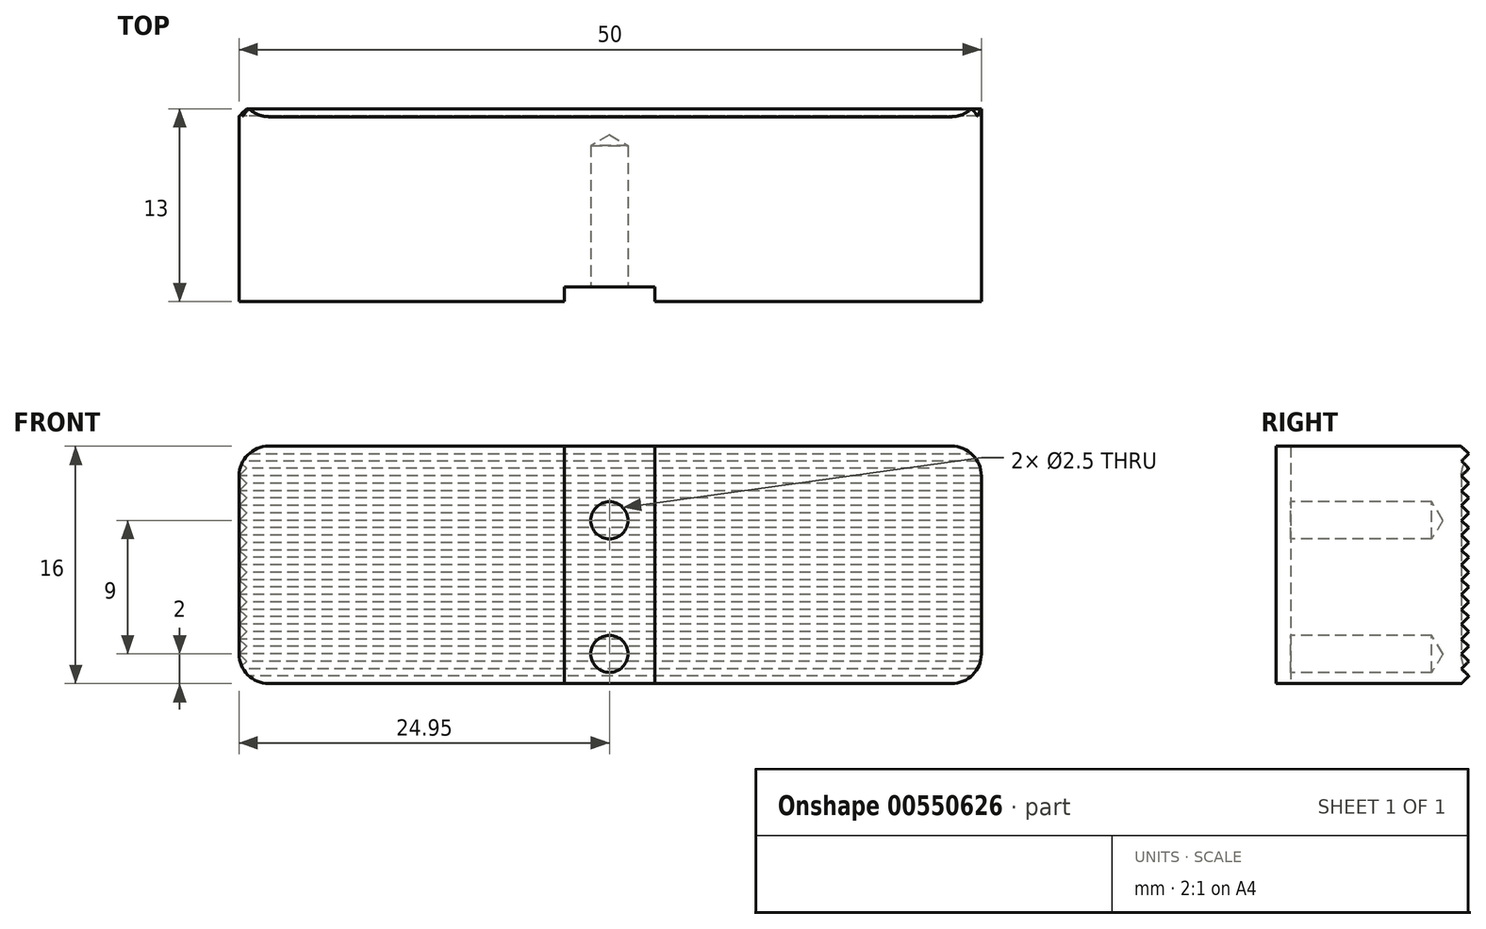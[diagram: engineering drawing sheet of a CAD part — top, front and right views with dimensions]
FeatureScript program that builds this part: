
annotation { "Feature Type Name" : "Feature", "Feature Type Description" : "" }
export const myFeature = defineFeature(function(context is Context, id is Id, definition is map)
    precondition{}
    {
        {
            var Q0;
            Q0=qCreatedBy(makeId("Front.planeOp"),FACE);
            var sketch = newSketch(context, id + "F0", { "sketchPlane" : qUnion([Q0])});
            skLineSegment(sketch, "E0.bottom", {"start": v(0, 0) * mm, "end": v(50, 0) * mm});
            skLineSegment(sketch, "E0.top", {"start": v(0, 16) * mm, "end": v(50, 16) * mm});
            skLineSegment(sketch, "E0.left", {"start": v(0, 0) * mm, "end": v(0, 16) * mm});
            skLineSegment(sketch, "E0.right", {"start": v(50, 0) * mm, "end": v(50, 16) * mm});
            skSolve(sketch);
        }
        {
            var Q0;
            Q0=makeQuery(id+"F0.imprint","IMPRINT",FACE,{"disambiguationData":[TD([[makeQuery(id+"F0.imprint","IMPRINT",EDGE,{"derivedFrom":sQuery(id+"F0.wireOp",EDGE,"E0.bottom")}),1.0]])]});
            extrude(context, id + "F1", {"entities" : qUnion([Q0]), "depth" : 13 * mm, "offsetDistance" : 25 * mm});
        }
        {
            var Q0;
            Q0=makeQuery(id+"F1.opExtrude","CAP_FACE",FACE,{"disambiguationData":[OSD([sQuery(id+"F0.wireOp",EDGE,"E0.bottom"),sQuery(id+"F0.wireOp",EDGE,"E0.top"),sQuery(id+"F0.wireOp",EDGE,"E0.left"),sQuery(id+"F0.wireOp",EDGE,"E0.right")])],"isStart":false});
            var sketch = newSketch(context, id + "F2", { "sketchPlane" : qUnion([Q0])});
            skLineSegment(sketch, "E1.bottom", {"start": v(21.9, 16) * mm, "end": v(28, 16) * mm});
            skLineSegment(sketch, "E1.top", {"start": v(21.9, -2) * mm, "end": v(28, -2) * mm});
            skLineSegment(sketch, "E1.left", {"start": v(21.9, 16) * mm, "end": v(21.9, -2) * mm});
            skLineSegment(sketch, "E1.right", {"start": v(28, 16) * mm, "end": v(28, -2) * mm});
            skSolve(sketch);
        }
        {
            var Q0;
            {var subQ0=sQuery(id+"F2.wireOp",EDGE,"E1.top");Q0=makeQuery(id+"F2.imprint","IMPRINT",FACE,{"disambiguationData":[TD([[makeQuery(id+"F2.imprint","IMPRINT",EDGE,{"derivedFrom":subQ0}),1.0]])]});}
            var Q1;
            {var subQ0=sQuery(id+"F2.wireOp",EDGE,"E1.bottom");Q1=makeQuery(id+"F2.imprint","IMPRINT",FACE,{"disambiguationData":[TD([[makeQuery(id+"F2.imprint","IMPRINT",EDGE,{"derivedFrom":subQ0}),-1.0]])]});}
            extrude(context, id + "F3", {"entities" : qUnion([Q0, Q1]), "operationType" : NewBodyOperationType.REMOVE, "oppositeDirection" : true, "depth" : 1 * mm, "offsetDistance" : 25 * mm});
        }
        {
            var Q0;
            Q0=makeQuery(id+"F3.boolean.opBoolean","COPY",FACE,{"derivedFrom":makeQuery(id+"F3.opExtrude","CAP_FACE",FACE,{"disambiguationData":[OSD([sQuery(id+"F2.wireOp",EDGE,"E1.bottom"),sQuery(id+"F2.wireOp",EDGE,"E1.top"),sQuery(id+"F2.wireOp",EDGE,"E1.left"),sQuery(id+"F2.wireOp",EDGE,"E1.right")])],"isStart":false})});
            var sketch = newSketch(context, id + "F4", { "sketchPlane" : qUnion([Q0])});
            skPoint(sketch, "E2", {"position": v(24.95, 11) * mm});
            skPoint(sketch, "E2.positionSnap0", {"position": v(24.95, 16) * mm});
            skPoint(sketch, "E3", {"position": v(24.95, 2) * mm});
            skSolve(sketch);
        }
        {
            var Q0;
            Q0=sQuery(id+"F4.wireOp",VERTEX,"E2");
            var Q1;
            Q1=sQuery(id+"F4.wireOp",VERTEX,"E3");
            var Q2;
            Q2=makeQuery(id+"F1.opExtrude","SWEPT_BODY",BODY,{"disambiguationData":[OSD([sQuery(id+"F0.wireOp",EDGE,"E0.bottom"),sQuery(id+"F0.wireOp",EDGE,"E0.top"),sQuery(id+"F0.wireOp",EDGE,"E0.left"),sQuery(id+"F0.wireOp",EDGE,"E0.right")])]});
            hole(context, id + "F5", {"style" : HoleStyle.SIMPLE, "endStyle" : HoleEndStyle.BLIND, "standardTappedOrClearance" : lookupTablePath({ "standard" : "ISO", "engagement" : "75%", "pitch" : "0.5 mm", "size" : "M3", "type" : "Tapped" }), "standardBlindInLast" : lookupTablePath({ "standard" : "ISO", "engagement" : "75%", "pitch" : "0.5 mm", "size" : "M3", "type" : "Tapped" }), "holeDiameter" : 2.5 * mm, "showTappedDepth" : true, "holeDepth" : 9.5 * mm, "isTappedThrough" : true, "tappedDepth" : 8 * mm, "tapClearance" : 3, "startFromSketch" : true, "locations" : qUnion([Q0, Q1]), "scope" : qUnion([Q2]), "majorDiameter" : 3 * mm});
        }
        {
            var Q0;
            Q0=makeQuery(id+"F1.opExtrude","CAP_EDGE",EDGE,{"disambiguationData":[OSD([sQuery(id+"F0.wireOp",EDGE,"E0.left")])],"isStart":true});
            var Q1;
            Q1=makeQuery(id+"F1.opExtrude","CAP_EDGE",EDGE,{"disambiguationData":[OSD([sQuery(id+"F0.wireOp",EDGE,"E0.top")])],"isStart":true});
            var Q2;
            Q2=makeQuery(id+"F1.opExtrude","CAP_EDGE",EDGE,{"disambiguationData":[OSD([sQuery(id+"F0.wireOp",EDGE,"E0.bottom")])],"isStart":true});
            chamfer(context, id + "F6", {"entities" : qUnion([Q0, Q1, Q2]), "width" : .5 * mm, "tangentPropagation" : true});
        }
        {
            var Q0;
            Q0=makeQuery(id+"F1.opExtrude","SWEPT_FACE",FACE,{"disambiguationData":[OSD([sQuery(id+"F0.wireOp",EDGE,"E0.left")])]});
            var sketch = newSketch(context, id + "F7", { "sketchPlane" : qUnion([Q0])});
            skPoint(sketch, "E4", {"position": v(0, 0.5) * mm});
            skPoint(sketch, "E5", {"position": v(0.5, 1) * mm});
            skPoint(sketch, "E6", {"position": v(0, 1.5) * mm});
            skPoint(sketch, "E7", {"position": v(0, 2.5) * mm});
            skPoint(sketch, "E8", {"position": v(0, 3.5) * mm});
            skPoint(sketch, "E9", {"position": v(0, 4.5) * mm});
            skPoint(sketch, "E10", {"position": v(0, 5.5) * mm});
            skPoint(sketch, "E11", {"position": v(0, 6.5) * mm});
            skPoint(sketch, "E12", {"position": v(0, 7.5) * mm});
            skPoint(sketch, "E13", {"position": v(0, 9.5) * mm});
            skPoint(sketch, "E14", {"position": v(0, 8.5) * mm});
            skPoint(sketch, "E15", {"position": v(0, 10.5) * mm});
            skPoint(sketch, "E16", {"position": v(0, 11.5) * mm});
            skPoint(sketch, "E17", {"position": v(0, 12.5) * mm});
            skPoint(sketch, "E18", {"position": v(0, 13.5) * mm});
            skPoint(sketch, "E19", {"position": v(0, 14.5) * mm});
            skPoint(sketch, "E20", {"position": v(0, 15.5) * mm});
            skPoint(sketch, "E21", {"position": v(0.5, 2) * mm});
            skPoint(sketch, "E22", {"position": v(0.5, 3) * mm});
            skPoint(sketch, "E23", {"position": v(0.5, 4) * mm});
            skPoint(sketch, "E24", {"position": v(0.5, 5) * mm});
            skPoint(sketch, "E25", {"position": v(0.5, 6) * mm});
            skPoint(sketch, "E26", {"position": v(0.5, 7) * mm});
            skPoint(sketch, "E27", {"position": v(0.5, 8) * mm});
            skPoint(sketch, "E28", {"position": v(0.5, 9) * mm});
            skPoint(sketch, "E29", {"position": v(0.5, 10) * mm});
            skPoint(sketch, "E30", {"position": v(0.5, 11) * mm});
            skPoint(sketch, "E31", {"position": v(0.5, 12) * mm});
            skPoint(sketch, "E32", {"position": v(0.5, 13) * mm});
            skPoint(sketch, "E33", {"position": v(0.5, 14) * mm});
            skPoint(sketch, "E34", {"position": v(0.5, 15) * mm});
            skPoint(sketch, "E35", {"position": v(0.53, 16) * mm});
            skPoint(sketch, "E36", {"position": v(0, 16.5) * mm});
            skLineSegment(sketch, "E37", {"start": v(0, 0.5) * mm, "end": v(0, 16.5) * mm});
            skLineSegment(sketch, "E38", {"start": v(0, 0.5) * mm, "end": v(0.5, 1) * mm});
            skLineSegment(sketch, "E39", {"start": v(0, 1.5) * mm, "end": v(0.5, 2) * mm});
            skLineSegment(sketch, "E40", {"start": v(0.5, 1) * mm, "end": v(0, 1.5) * mm});
            skLineSegment(sketch, "E41", {"start": v(0, 2.5) * mm, "end": v(0.5, 3) * mm});
            skLineSegment(sketch, "E42", {"start": v(0.5, 2) * mm, "end": v(0, 2.5) * mm});
            skLineSegment(sketch, "E43", {"start": v(0.5, 3) * mm, "end": v(0, 3.5) * mm});
            skLineSegment(sketch, "E44", {"start": v(0.5, 4) * mm, "end": v(0, 4.5) * mm});
            skLineSegment(sketch, "E45", {"start": v(0, 3.5) * mm, "end": v(0.5, 4) * mm});
            skLineSegment(sketch, "E46", {"start": v(0, 4.5) * mm, "end": v(0.5, 5) * mm});
            skLineSegment(sketch, "E47", {"start": v(0.5, 5) * mm, "end": v(0, 5.5) * mm});
            skLineSegment(sketch, "E48", {"start": v(0, 5.5) * mm, "end": v(0.5, 6) * mm});
            skLineSegment(sketch, "E49", {"start": v(0.5, 6) * mm, "end": v(0, 6.5) * mm});
            skLineSegment(sketch, "E50", {"start": v(0, 6.5) * mm, "end": v(0.5, 7) * mm});
            skLineSegment(sketch, "E51", {"start": v(0.5, 7) * mm, "end": v(0, 7.5) * mm});
            skLineSegment(sketch, "E52", {"start": v(0, 7.5) * mm, "end": v(0.5, 8) * mm});
            skLineSegment(sketch, "E53", {"start": v(0.5, 8) * mm, "end": v(0, 8.5) * mm});
            skLineSegment(sketch, "E54", {"start": v(0, 8.5) * mm, "end": v(0.5, 9) * mm});
            skLineSegment(sketch, "E55", {"start": v(0.5, 9) * mm, "end": v(0, 9.5) * mm});
            skLineSegment(sketch, "E56", {"start": v(0, 9.5) * mm, "end": v(0.5, 10) * mm});
            skLineSegment(sketch, "E57", {"start": v(0.5, 10) * mm, "end": v(0, 10.5) * mm});
            skLineSegment(sketch, "E58", {"start": v(0, 10.5) * mm, "end": v(0.5, 11) * mm});
            skLineSegment(sketch, "E59", {"start": v(0.5, 11) * mm, "end": v(0, 11.5) * mm});
            skLineSegment(sketch, "E60", {"start": v(0, 11.5) * mm, "end": v(0.5, 12) * mm});
            skLineSegment(sketch, "E61", {"start": v(0.5, 12) * mm, "end": v(0, 12.5) * mm});
            skLineSegment(sketch, "E62", {"start": v(0, 12.5) * mm, "end": v(0.5, 13) * mm});
            skLineSegment(sketch, "E63", {"start": v(0.5, 13) * mm, "end": v(0, 13.5) * mm});
            skLineSegment(sketch, "E64", {"start": v(0, 13.5) * mm, "end": v(0.5, 14) * mm});
            skLineSegment(sketch, "E65", {"start": v(0.5, 14) * mm, "end": v(0, 14.5) * mm});
            skLineSegment(sketch, "E66", {"start": v(0, 14.5) * mm, "end": v(0.5, 15) * mm});
            skLineSegment(sketch, "E67", {"start": v(0, 15.5) * mm, "end": v(0.5, 15) * mm});
            skLineSegment(sketch, "E68", {"start": v(0, 15.5) * mm, "end": v(0.53, 16) * mm});
            skLineSegment(sketch, "E69", {"start": v(0.53, 16) * mm, "end": v(0, 16.5) * mm});
            skSolve(sketch);
        }
        {
            var Q0;
            {var subQ0=sQuery(id+"F7.wireOp",EDGE,"E41");Q0=makeQuery(id+"F7.imprint","IMPRINT",FACE,{"disambiguationData":[TD([[makeQuery(id+"F7.imprint","IMPRINT",EDGE,{"derivedFrom":subQ0}),1.0]])]});}
            var Q1;
            {var subQ2=sQuery(id+"F7.wireOp",EDGE,"E44");Q1=makeQuery(id+"F7.imprint","IMPRINT",FACE,{"disambiguationData":[TD([[makeQuery(id+"F7.imprint","IMPRINT",EDGE,{"derivedFrom":subQ2}),1.0]])]});}
            var Q2;
            {var subQ0=sQuery(id+"F7.wireOp",EDGE,"E46");Q2=makeQuery(id+"F7.imprint","IMPRINT",FACE,{"disambiguationData":[TD([[makeQuery(id+"F7.imprint","IMPRINT",EDGE,{"derivedFrom":subQ0}),1.0]])]});}
            var Q3;
            {var subQ0=sQuery(id+"F7.wireOp",EDGE,"E48");Q3=makeQuery(id+"F7.imprint","IMPRINT",FACE,{"disambiguationData":[TD([[makeQuery(id+"F7.imprint","IMPRINT",EDGE,{"derivedFrom":subQ0}),1.0]])]});}
            var Q4;
            {var subQ0=sQuery(id+"F7.wireOp",EDGE,"E50");Q4=makeQuery(id+"F7.imprint","IMPRINT",FACE,{"disambiguationData":[TD([[makeQuery(id+"F7.imprint","IMPRINT",EDGE,{"derivedFrom":subQ0}),1.0]])]});}
            var Q5;
            {var subQ0=sQuery(id+"F7.wireOp",EDGE,"E52");Q5=makeQuery(id+"F7.imprint","IMPRINT",FACE,{"disambiguationData":[TD([[makeQuery(id+"F7.imprint","IMPRINT",EDGE,{"derivedFrom":subQ0}),1.0]])]});}
            var Q6;
            {var subQ0=sQuery(id+"F7.wireOp",EDGE,"E54");Q6=makeQuery(id+"F7.imprint","IMPRINT",FACE,{"disambiguationData":[TD([[makeQuery(id+"F7.imprint","IMPRINT",EDGE,{"derivedFrom":subQ0}),1.0]])]});}
            var Q7;
            {var subQ0=sQuery(id+"F7.wireOp",EDGE,"E56");Q7=makeQuery(id+"F7.imprint","IMPRINT",FACE,{"disambiguationData":[TD([[makeQuery(id+"F7.imprint","IMPRINT",EDGE,{"derivedFrom":subQ0}),1.0]])]});}
            var Q8;
            {var subQ0=sQuery(id+"F7.wireOp",EDGE,"E58");Q8=makeQuery(id+"F7.imprint","IMPRINT",FACE,{"disambiguationData":[TD([[makeQuery(id+"F7.imprint","IMPRINT",EDGE,{"derivedFrom":subQ0}),1.0]])]});}
            var Q9;
            {var subQ0=sQuery(id+"F7.wireOp",EDGE,"E60");Q9=makeQuery(id+"F7.imprint","IMPRINT",FACE,{"disambiguationData":[TD([[makeQuery(id+"F7.imprint","IMPRINT",EDGE,{"derivedFrom":subQ0}),1.0]])]});}
            var Q10;
            {var subQ0=sQuery(id+"F7.wireOp",EDGE,"E62");Q10=makeQuery(id+"F7.imprint","IMPRINT",FACE,{"disambiguationData":[TD([[makeQuery(id+"F7.imprint","IMPRINT",EDGE,{"derivedFrom":subQ0}),1.0]])]});}
            var Q11;
            {var subQ0=sQuery(id+"F7.wireOp",EDGE,"E64");Q11=makeQuery(id+"F7.imprint","IMPRINT",FACE,{"disambiguationData":[TD([[makeQuery(id+"F7.imprint","IMPRINT",EDGE,{"derivedFrom":subQ0}),1.0]])]});}
            var Q12;
            {var subQ0=sQuery(id+"F7.wireOp",EDGE,"E66");Q12=makeQuery(id+"F7.imprint","IMPRINT",FACE,{"disambiguationData":[TD([[makeQuery(id+"F7.imprint","IMPRINT",EDGE,{"derivedFrom":subQ0}),1.0]])]});}
            var Q13;
            {var subQ3=sQuery(id+"F7.wireOp",EDGE,"E69");Q13=makeQuery(id+"F7.imprint","IMPRINT",FACE,{"disambiguationData":[TD([[makeQuery(id+"F7.imprint","IMPRINT",EDGE,{"derivedFrom":subQ3}),1.0]])]});}
            var Q14;
            {var subQ3=sQuery(id+"F7.wireOp",EDGE,"E68");Q14=makeQuery(id+"F7.imprint","IMPRINT",FACE,{"disambiguationData":[TD([[makeQuery(id+"F7.imprint","IMPRINT",EDGE,{"derivedFrom":subQ3}),1.0]])]});}
            var Q15;
            {var subQ0=sQuery(id+"F7.wireOp",EDGE,"E38");Q15=makeQuery(id+"F7.imprint","IMPRINT",FACE,{"disambiguationData":[TD([[makeQuery(id+"F7.imprint","IMPRINT",EDGE,{"derivedFrom":subQ0}),1.0]])]});}
            extrude(context, id + "F8", {"entities" : qUnion([Q0, Q1, Q2, Q3, Q4, Q5, Q6, Q7, Q8, Q9, Q10, Q11, Q12, Q13, Q14, Q15]), "operationType" : NewBodyOperationType.REMOVE, "endBound" : BoundingType.THROUGH_ALL, "oppositeDirection" : true, "depth" : 50 * mm, "offsetDistance" : 25 * mm});
        }
        {
            var Q0;
            {var subQ0=sQuery(id+"F7.wireOp",EDGE,"E39");Q0=makeQuery(id+"F7.imprint","IMPRINT",FACE,{"disambiguationData":[TD([[makeQuery(id+"F7.imprint","IMPRINT",EDGE,{"derivedFrom":subQ0}),1.0]])]});}
            extrude(context, id + "F9", {"entities" : qUnion([Q0]), "operationType" : NewBodyOperationType.REMOVE, "endBound" : BoundingType.THROUGH_ALL, "oppositeDirection" : true, "depth" : 25 * mm, "offsetDistance" : 25 * mm});
        }
        {
            var Q0;
            Q0=makeQuery(id+"F1.opExtrude","SWEPT_EDGE",EDGE,{"disambiguationData":[OSD([sQuery(id+"F0.wireOp",EDGE,"E0.top"),sQuery(id+"F0.wireOp",EDGE,"E0.right")])]});
            var Q1;
            Q1=makeQuery(id+"F1.opExtrude","SWEPT_EDGE",EDGE,{"disambiguationData":[OSD([sQuery(id+"F0.wireOp",EDGE,"E0.bottom"),sQuery(id+"F0.wireOp",EDGE,"E0.right")])]});
            var Q2;
            Q2=makeQuery(id+"F1.opExtrude","SWEPT_EDGE",EDGE,{"disambiguationData":[OSD([sQuery(id+"F0.wireOp",EDGE,"E0.top"),sQuery(id+"F0.wireOp",EDGE,"E0.left")])]});
            var Q3;
            Q3=makeQuery(id+"F1.opExtrude","SWEPT_EDGE",EDGE,{"disambiguationData":[OSD([sQuery(id+"F0.wireOp",EDGE,"E0.bottom"),sQuery(id+"F0.wireOp",EDGE,"E0.left")])]});
            fillet(context, id + "F10", {"entities" : qUnion([Q0, Q1, Q2, Q3]), "radius" : 2 * mm, "tangentPropagation" : true, "allowEdgeOverflow" : false});
        }
    });
